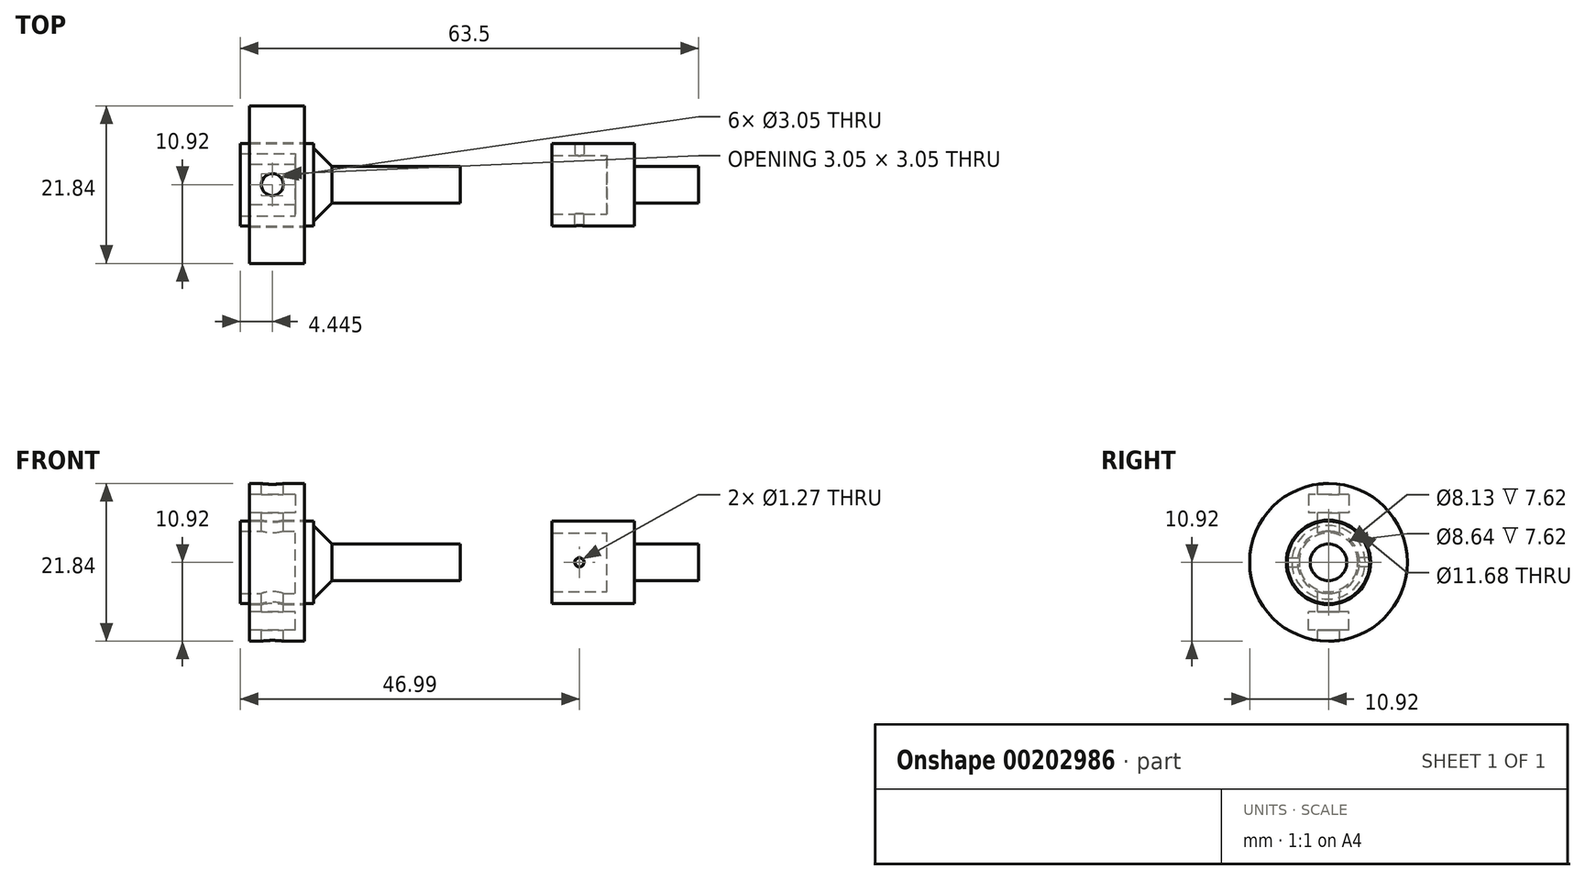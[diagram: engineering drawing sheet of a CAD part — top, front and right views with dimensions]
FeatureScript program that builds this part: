
annotation { "Feature Type Name" : "Feature", "Feature Type Description" : "" }
export const myFeature = defineFeature(function(context is Context, id is Id, definition is map)
    precondition{}
    {
        {
            var Q0;
            Q0=qCreatedBy(makeId("Top.planeOp"),FACE);
            var sketch = newSketch(context, id + "F0", { "sketchPlane" : qUnion([Q0])});
            skLineSegment(sketch, "E0.bottom", {"start": v(-20.32, 5.71) * mm, "end": v(-8.9, 5.72) * mm});
            skLineSegment(sketch, "E0.left", {"start": v(-20.32, 5.71) * mm, "end": v(-20.32, 4.06) * mm});
            skPoint(sketch, "E0.middle", {"position": v(0, 0) * mm});
            skLineSegment(sketch, "E1", {"start": v(95.72, 0) * mm, "end": v(-119.84, 0) * mm, "construction": true});
            skPoint(sketch, "E0.top.start.orphan", {"position": v(-20.32, -11.43) * mm});
            skLineSegment(sketch, "E2", {"start": v(-20.32, 4.06) * mm, "end": v(-12.7, 4.06) * mm});
            skLineSegment(sketch, "E3", {"start": v(-12.7, 4.06) * mm, "end": v(-12.7, 0) * mm});
            skLineSegment(sketch, "E4", {"start": v(-8.9, 5.72) * mm, "end": v(-8.9, 2.54) * mm});
            skLineSegment(sketch, "E5", {"start": v(-8.9, 2.54) * mm, "end": v(0, 2.54) * mm});
            skLineSegment(sketch, "E6", {"start": v(0, 2.54) * mm, "end": v(0, 0) * mm});
            skLineSegment(sketch, "E7", {"start": v(0, 0) * mm, "end": v(-12.7, 0) * mm});
            skLineSegment(sketch, "E8", {"start": v(-53.34, 5.71) * mm, "end": v(-63.5, 5.71) * mm});
            skLineSegment(sketch, "E9", {"start": v(-33.02, 2.54) * mm, "end": v(-53.34, 2.54) * mm});
            skLineSegment(sketch, "E10", {"start": v(-33.02, 0) * mm, "end": v(-55.88, 0) * mm});
            skLineSegment(sketch, "E11", {"start": v(-55.88, 0) * mm, "end": v(-55.88, 4.32) * mm});
            skLineSegment(sketch, "E12", {"start": v(-55.88, 4.32) * mm, "end": v(-63.5, 4.32) * mm});
            skLineSegment(sketch, "E13", {"start": v(-63.5, 4.32) * mm, "end": v(-63.5, 5.71) * mm});
            skLineSegment(sketch, "E14", {"start": v(-55.88, 0) * mm, "end": v(-33.02, 0) * mm});
            skLineSegment(sketch, "E15", {"start": v(-33.02, 2.54) * mm, "end": v(-33.02, 0) * mm});
            skLineSegment(sketch, "E16", {"start": v(-33.02, 0) * mm, "end": v(-33.02, 0) * mm});
            skLineSegment(sketch, "E17", {"start": v(-53.34, 2.54) * mm, "end": v(-53.34, 5.71) * mm});
            skLineSegment(sketch, "E18.bottom", {"start": v(-62.23, 10.92) * mm, "end": v(-54.6, 10.92) * mm});
            skLineSegment(sketch, "E18.top", {"start": v(-62.23, 5.84) * mm, "end": v(-54.6, 5.84) * mm});
            skLineSegment(sketch, "E18.left", {"start": v(-62.23, 10.92) * mm, "end": v(-62.23, 5.84) * mm});
            skLineSegment(sketch, "E18.right", {"start": v(-54.6, 10.92) * mm, "end": v(-54.6, 5.84) * mm});
            skSolve(sketch);
        }
        {
            var Q0;
            Q0=makeQuery(id+"F0.imprint","IMPRINT",FACE,{"disambiguationData":[TD([[makeQuery(id+"F0.imprint","IMPRINT",EDGE,{"derivedFrom":sQuery(id+"F0.wireOp",EDGE,"E0.bottom")}),-1.0]])]});
            var Q1;
            Q1=makeQuery(id+"F0.imprint","IMPRINT",FACE,{"disambiguationData":[TD([[makeQuery(id+"F0.imprint","IMPRINT",EDGE,{"derivedFrom":sQuery(id+"F0.wireOp",EDGE,"E8")}),1.0]])]});
            var Q2;
            Q2=sQuery(id+"F0.wireOp",EDGE,"E1");
            revolve(context, id + "F1", {"entities" : qUnion([Q0, Q1]), "axis" : qUnion([Q2]), "revolveType" : RevolveType.FULL});
        }
        {
            var Q0;
            Q0=qCreatedBy(makeId("Front.planeOp"),FACE);
            var sketch = newSketch(context, id + "F2", { "sketchPlane" : qUnion([Q0])});
            skLineSegment(sketch, "E19", {"start": v(2.12, 0) * mm, "end": v(-14.75, 0) * mm, "construction": true});
            skCircle(sketch, "E20", {"center": v(-16.51, 0) * mm, "radius": 0.64 * mm});
            skSolve(sketch);
        }
        {
            var Q0;
            Q0 = qSketchRegion(id + "F2", true);
            extrude(context, id + "F3", {"entities" : qUnion([Q0]), "operationType" : NewBodyOperationType.REMOVE, "endBound" : BoundingType.THROUGH_ALL, "oppositeDirection" : true, "depth" : 25.4 * mm});
        }
        {
            var Q0;
            Q0 = qSketchRegion(id + "F2", true);
            extrude(context, id + "F4", {"entities" : qUnion([Q0]), "operationType" : NewBodyOperationType.REMOVE, "endBound" : BoundingType.THROUGH_ALL, "depth" : 25.4 * mm});
        }
        {
            var Q0;
            Q0=makeQuery(id+"F1.opRevolve","SWEPT_EDGE",EDGE,{"disambiguationData":[OSD([sQuery(id+"F0.wireOp",EDGE,"E9"),sQuery(id+"F0.wireOp",EDGE,"E17")])]});
            chamfer(context, id + "F5", {"entities" : qUnion([Q0]), "width" : 2.54 * mm, "tangentPropagation" : true});
        }
        {
            var Q0;
            Q0=makeQuery(id+"F0.imprint","IMPRINT",FACE,{"disambiguationData":[TD([[makeQuery(id+"F0.imprint","IMPRINT",EDGE,{"derivedFrom":sQuery(id+"F0.wireOp",EDGE,"E18.bottom")}),-1.0]])]});
            var Q1;
            Q1=sQuery(id+"F0.wireOp",EDGE,"E1");
            revolve(context, id + "F6", {"entities" : qUnion([Q0]), "axis" : qUnion([Q1]), "revolveType" : RevolveType.FULL});
        }
        {
            var Q0;
            Q0=makeQuery(id+"F6.opRevolve","SWEPT_FACE",FACE,{"disambiguationData":[OSD([sQuery(id+"F0.wireOp",EDGE,"E18.left")])]});
            var sketch = newSketch(context, id + "F7", { "sketchPlane" : qUnion([Q0])});
            skLineSegment(sketch, "E21", {"start": v(0, 13.73) * mm, "end": v(0, -14.98) * mm, "construction": true});
            skLineSegment(sketch, "E22.bottom", {"start": v(-2.8, 9.4) * mm, "end": v(2.8, 9.4) * mm});
            skLineSegment(sketch, "E22.top", {"start": v(-2.8, 6.86) * mm, "end": v(2.8, 6.86) * mm});
            skLineSegment(sketch, "E22.left", {"start": v(-2.8, 9.4) * mm, "end": v(-2.8, 6.86) * mm});
            skLineSegment(sketch, "E22.right", {"start": v(2.8, 9.4) * mm, "end": v(2.8, 6.86) * mm});
            skLineSegment(sketch, "E23", {"start": v(-14.23, 0) * mm, "end": v(18.82, 0) * mm, "construction": true});
            skLineSegment(sketch, "E24.MirrorCS", {"start": v(2.8, -9.4) * mm, "end": v(2.8, -6.86) * mm});
            skLineSegment(sketch, "E25.MirrorCS", {"start": v(-2.8, -9.4) * mm, "end": v(-2.8, -6.86) * mm});
            skLineSegment(sketch, "E26.MirrorCS", {"start": v(-2.8, -6.86) * mm, "end": v(2.8, -6.86) * mm});
            skLineSegment(sketch, "E27.MirrorCS", {"start": v(-2.8, -9.4) * mm, "end": v(2.8, -9.4) * mm});
            skSolve(sketch);
        }
        {
            var Q0;
            Q0 = qSketchRegion(id + "F7", true);
            extrude(context, id + "F8", {"entities" : qUnion([Q0]), "operationType" : NewBodyOperationType.REMOVE, "oppositeDirection" : true, "depth" : 6.35 * mm});
        }
        {
            var Q0;
            Q0=qCreatedBy(makeId("Top.planeOp"),FACE);
            var sketch = newSketch(context, id + "F9", { "sketchPlane" : qUnion([Q0])});
            skCircle(sketch, "E28", {"center": v(-59.06, 0) * mm, "radius": 1.52 * mm});
            skSolve(sketch);
        }
        {
            var Q0;
            Q0=makeQuery(id+"F9.imprint","IMPRINT",FACE,{"disambiguationData":[TD([[makeQuery(id+"F9.imprint","IMPRINT",EDGE,{"derivedFrom":sQuery(id+"F9.wireOp",EDGE,"E28")}),1.0]])]});
            extrude(context, id + "F10", {"entities" : qUnion([Q0]), "operationType" : NewBodyOperationType.REMOVE, "endBound" : BoundingType.THROUGH_ALL, "oppositeDirection" : true, "depth" : 25.4 * mm, "hasSecondDirection" : true, "secondDirectionBound" : BoundingType.THROUGH_ALL, "secondDirectionOppositeDirection" : false, "secondDirectionDepth" : 25.4 * mm});
        }
    });
